# Revit family: Nuaire_IfcFanType_Faith-plus5
name_source: partatom
category: Mechanical Equipment
revit_build: Autodesk Revit 2018 (Build: 20170223_1515(x64)
units: mm (PartAtom-declared; Revit-internal decimal feet)

## family parameters
Always vertical = Yes
Cut with Voids When Loaded = No
OmniClass Number = 23.75.00.00
OmniClass Title = Climate Control (HVAC)
Part Type = Normal
Room Calculation Point = No
Round Connector Dimension = Use Radius
Shared = No
Work Plane-Based = No

## types (2) — shared parameters
6 Monthly = SFG20 20-06
Annually = SFG20 20-06
BMS Links = No
Battery Supply = No
Bespoke Timeframe = SFG20 20-06
CE Approval = Yes
COBie.Type = Yes
COBie.Type.Category = Pr_65_67_29_12 : Centrifugal Fans
COBie.Type.Length = 46 mm  [stored 0.150919 ft]
COBie.Type.Manufacturer = Nuaire
COBie.Type.NominalHeight = 164 mm  [stored 0.538058 ft]
COBie.Type.NominalLength = 46 mm  [stored 0.150919 ft]
COBie.Type.NominalWidth = 164 mm  [stored 0.538058 ft]
COBie.Type.WarrantyDescription = 5 years.  First year parts and labour, remaining 4 years parts only.
COBie.Type.WarrantyDurationLabor = 1
COBie.Type.WarrantyDurationParts = 5
COBie.Type.WarrantyDurationUnit = Year
COBie.Type.WarrantyGuarantorLabor = Nuaire
COBie.Type.WarrantyGuarantorParts = Nuaire
Catalogue Pages = https://www.nuaire.co.uk
Classification.Uniclass.Pr.Description = Mixed flow fans
Classification.Uniclass.Pr.Number = Pr_65_67_29_52
Daily = SFG20 20-06
Environmental Product Declaration = WEEE, RoHS
Fax Number = +44(0)2920-858-222
Fire Control Panel Links = No
Frequency = 50.00 Hz
Full Load Current = 0.060 A
Height = 164 mm  [stored 0.538058 ft]
I&M Manual = https://www.nuaire.co.uk
IFCExportAs = IfcFanType
IFCExportType = NOTDEFINED
Length = 46 mm  [stored 0.150919 ft]
Location of Manufacturer = 51.571856, -3.232638
Maintenance Required 0 to 300hrs = https://www.nuaire.co.uk
Maintenance Required 1001 to 2000hrs = https://www.nuaire.co.uk
Maintenance Required 2001 to 4000hrs = https://www.nuaire.co.uk
Maintenance Required 301 to 600hrs = https://www.nuaire.co.uk
Maintenance Required 4001 to 8000hrs = https://www.nuaire.co.uk
Maintenance Required 601 to 1000hrs = https://www.nuaire.co.uk
Maintenance Required 8001 to 12000hrs = https://www.nuaire.co.uk
Manufacturer = Nuaire
Manufacturer Website = http://www.nuaire.co.uk
Maximum Ambient Temperature = 40.00 °C
Monthly = SFG20 20-06
Nominal Motor Rating = 0.006 kW
Nominal Motor Speed (rpm) = 2700
Number of Connection Poles = 2
OmniClass Number = 23-33 31 19
OmniClass Title = Fans
Operation and Maintenance Manual = https://www.nuaire.co.uk
Postcode = CF83 1NA
Power Source = Mains
Product Literature = https://www.nuaire.co.uk
Product Range = Faith
Quarterly = SFG20 20-06
Reference Standard = ISO 9001:2015
Responsible Sourcing of Materials = FSC
Revit Family Last Revised = 2023-10-24T11:21:00
Spigot Diameter = 100 mm  [stored 0.328084 ft]
Spigot Radius = 50 mm  [stored 0.164042 ft]
Starting Current = 0.300 A
Supply Phase = 1
Telephone Number = +44(0)2920-858-200
Type Comments = 1
URL = http://www.nuaire.co.uk
Weatherproof or Internal Only = Internal
Weekly = SFG20 20-06
Weight = 0.58 kg
Width = 164 mm  [stored 0.538058 ft]
zero-valued in all types: COBie.Type.Area, COBie.Type.ReplacementCost, Life Cycle Analysis

## per-type parameters (varying)
| type | Apparent Load | COBie.Type.Description | COBie.Type.DurationUnit | Description | Voltage |
| FAITH-PLUS | 13.80 VA | 230V Continuous Mixed Flow Extract Fan |  | 230V Continuous Mixed Flow Extract Fan | 230.00 V |
| FAITH-SELV-PLUS | 1.44 VA | 24V Continuous Mixed Flow Extract Fan | Year | 24V Continuous Mixed Flow Extract Fan | 24.00 V |

note: column(s) folded — value = type name in every type: COBie.Type.ModelNumber, COBie.Type.ModelReference, COBie.Type.Name, Model

note: [stored X ft] marks values corroborated as IEEE doubles in the binary element streams (Revit-internal decimal feet)

## geometry (parser evidence)
native form markers: Blend x8, Sweep x14
no freeform markers — native parametric forms only
